# Revit family: 820-00-024 DN350-400
name_source: partatom
category: Pipe Accessories
units: mm (PartAtom-declared; Revit-internal decimal feet)

## family parameters
Always vertical = Yes
Cut with Voids When Loaded = No
Part Type = Valve - Breaks Into
Round Connector Dimension = Use Diameter
Shared = No
Work Plane-Based = No

## types (2) — shared parameters
1 = 1 mm  [stored 0.00328084 ft]
90 = 90 mm  [stored 0.295276 ft]
Actuator_Dia = 150 mm  [stored 0.492126 ft]
Body_wallthickness = 10 mm  [stored 0.0328084 ft]
DN350_PN10/16 = 820-0350-00-02020160002
DN400_PN10/16 = 820-0400-00-02020160002
Description_ = AVK CENTRIC BUTTERFLY VALVE WAFER TYPE, PN10/16
F2 = 40 mm  [stored 0.131234 ft]
FL_T = 15 mm  [stored 0.0492126 ft]
Flange_thickness = 11 mm  [stored 0.0360892 ft]
Hole_L = 75 mm  [stored 0.246063 ft]
Search_table = 820-00-024 DN350-400
URL product pages = https://www.avkvalves.com
Width_dim = 128 mm  [stored 0.419948 ft]
fillet = 20 mm  [stored 0.0656168 ft]
fillte1 = 10 mm  [stored 0.0328084 ft]
zero-valued in all types: Default Elevation

## per-type parameters (varying)
- DN350_PN10/16: Bore=175 mm  [stored 0.574147 ft]; DN=350 mm; EPDM=174 mm  [stored 0.570866 ft]; EPDM_R=191 mm; F=22 mm  [stored 0.0721785 ft]; FL_R=185 mm  [stored 0.606955 ft]; Fillet=26 mm; H2=268 mm; Hole_L1=224 mm; Hole_dia=26 mm; ID=175 mm  [stored 0.574147 ft]; L=80 mm  [stored 0.262467 ft]; L-2=78 mm  [stored 0.255906 ft]; L2=213 mm; LUG_T=39 mm  [stored 0.127953 ft]; L_ref=56 mm  [stored 0.183727 ft]; L_ref_2=112 mm  [stored 0.367454 ft]; L_ref_3=47 mm; Lug_D=18 mm; PCD=235 mm; W2_ref=330 mm; Wafer_Dim2=249 mm; Wafer_dim=85 mm  [stored 0.278871 ft]; Wafer_dim1=276 mm; disk=29 mm  [stored 0.0951444 ft]
- DN400_PN10/16: Bore=200 mm  [stored 0.656168 ft]; DN=400 mm; EPDM=199 mm  [stored 0.652887 ft]; EPDM_R=214 mm; F=27 mm  [stored 0.0885827 ft]; FL_R=210 mm  [stored 0.688976 ft]; Fillet=28 mm  [stored 0.0918635 ft]; H2=299 mm; Hole_L1=250 mm; Hole_dia=28 mm  [stored 0.0918635 ft]; ID=200 mm  [stored 0.656168 ft]; L=102 mm  [stored 0.334646 ft]; L-2=100 mm  [stored 0.328084 ft]; L2=238 mm; LUG_T=50 mm  [stored 0.164042 ft]; L_ref=78 mm  [stored 0.255906 ft]; L_ref_2=156 mm  [stored 0.511811 ft]; L_ref_3=65 mm  [stored 0.213255 ft]; Lug_D=20 mm  [stored 0.0656168 ft]; PCD=263 mm; W2_ref=365 mm; Wafer_Dim2=278 mm; Wafer_dim=95 mm; Wafer_dim1=309 mm; disk=38 mm

note: [stored X ft] marks values corroborated as IEEE doubles in the binary element streams (Revit-internal decimal feet)

## geometry (parser evidence)
native form markers: Sweep x4
no freeform markers — native parametric forms only
